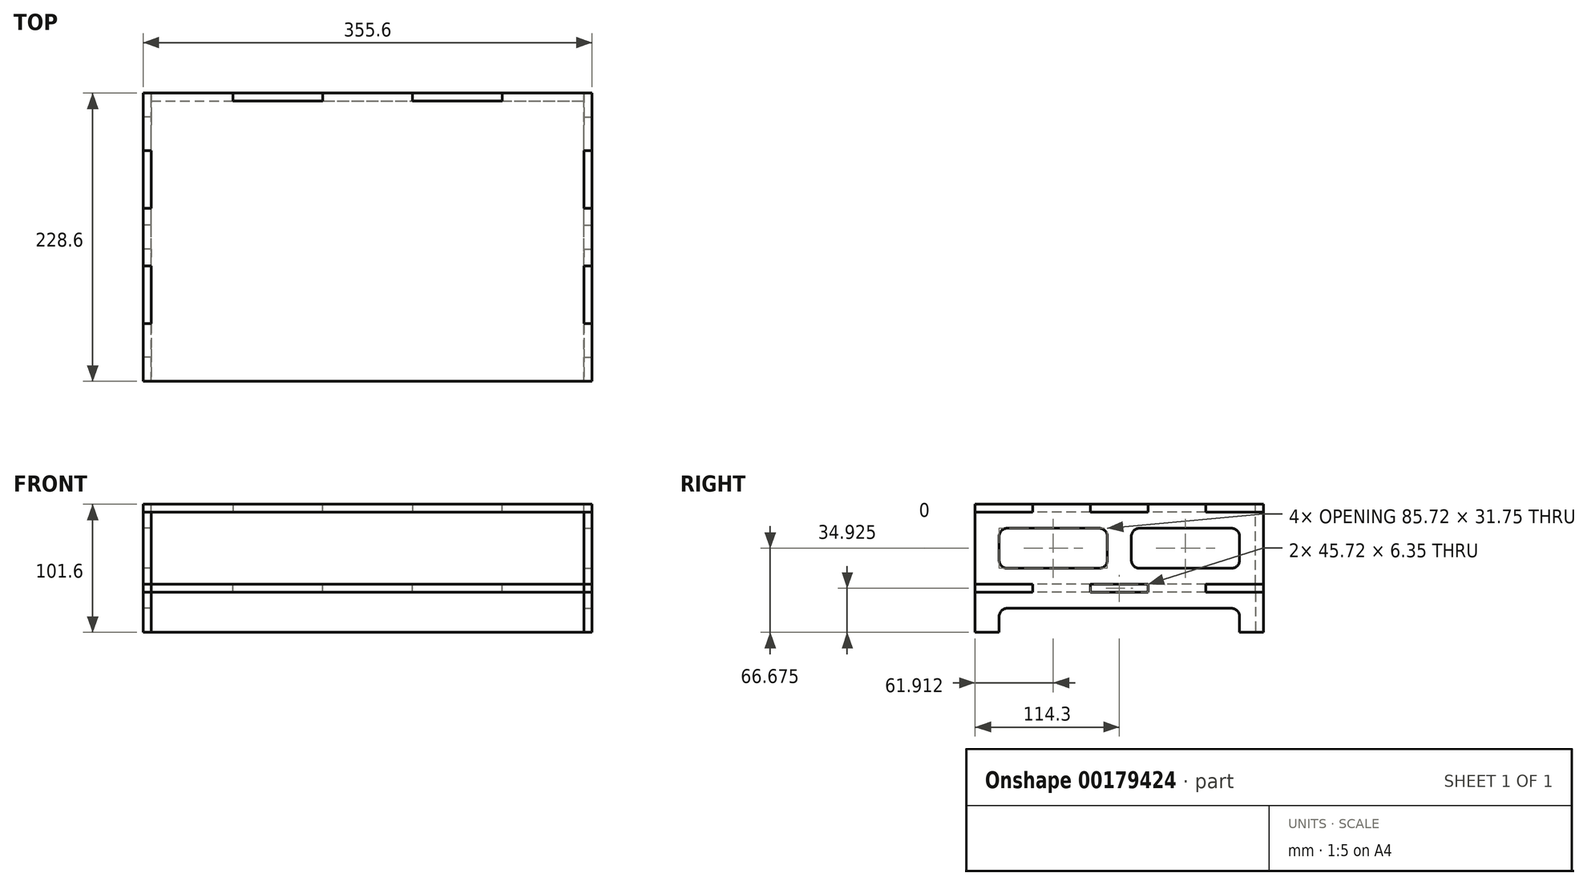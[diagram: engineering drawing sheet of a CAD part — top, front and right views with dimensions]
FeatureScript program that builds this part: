
annotation { "Feature Type Name" : "Feature", "Feature Type Description" : "" }
export const myFeature = defineFeature(function(context is Context, id is Id, definition is map)
    precondition{}
    {
        {
            var Q0;
            Q0=qCreatedBy(makeId("Top.planeOp"),FACE);
            var sketch = newSketch(context, id + "F0", { "sketchPlane" : qUnion([Q0])});
            skLineSegment(sketch, "E0.rect.bottom", {"start": v(177.8, -114.3) * mm, "end": v(-177.8, -114.3) * mm});
            skLineSegment(sketch, "E0.rect.top", {"start": v(177.8, 114.3) * mm, "end": v(-177.8, 114.3) * mm});
            skLineSegment(sketch, "E0.rect.left", {"start": v(177.8, -114.3) * mm, "end": v(177.8, 114.3) * mm});
            skLineSegment(sketch, "E0.rect.right", {"start": v(-177.8, -114.3) * mm, "end": v(-177.8, 114.3) * mm});
            skPoint(sketch, "E0.rect.middle", {"position": v(0, 0) * mm});
            skSolve(sketch);
        }
        {
            var Q0;
            Q0=qCreatedBy(makeId("Right.planeOp"),FACE);
            var sketch = newSketch(context, id + "F1", { "sketchPlane" : qUnion([Q0])});
            skLineSegment(sketch, "E1.0", {"start": v(-114.3, 0) * mm, "end": v(114.3, 0) * mm});
            skLineSegment(sketch, "E2", {"start": v(114.3, 0) * mm, "end": v(114.3, -101.6) * mm});
            skLineSegment(sketch, "E3", {"start": v(114.3, -101.6) * mm, "end": v(-114.3, -101.6) * mm});
            skLineSegment(sketch, "E4", {"start": v(-114.3, -101.6) * mm, "end": v(-114.3, 0) * mm});
            skLineSegment(sketch, "E5", {"start": v(-114.3, -63.5) * mm, "end": v(114.3, -63.5) * mm});
            skSolve(sketch);
        }
        {
            var Q0;
            Q0=sQuery(id+"F0.wireOp",EDGE,"E0.rect.top");
            cPlane(context, id + "F2", {"entities" : qUnion([Q0]), "cplaneType" : CPlaneType.LINE_ANGLE, "offset" : 152.4 * mm, "angle" : 0 * degree, "width" : 152.4 * mm, "height" : 152.4 * mm});
        }
        {
            var Q0;
            Q0=qCreatedBy(makeId("Top.planeOp"),FACE);
            var sketch = newSketch(context, id + "F3", { "sketchPlane" : qUnion([Q0])});
            skLineSegment(sketch, "E6.0", {"start": v(177.8, -114.3) * mm, "end": v(-177.8, -114.3) * mm});
            skLineSegment(sketch, "E7.0", {"start": v(-177.8, -114.3) * mm, "end": v(-177.8, -68.58) * mm});
            skLineSegment(sketch, "E8.0", {"start": v(177.8, -114.3) * mm, "end": v(177.8, -68.58) * mm});
            skLineSegment(sketch, "E9", {"start": v(-177.8, 114.3) * mm, "end": v(-177.8, 68.58) * mm});
            skLineSegment(sketch, "E10", {"start": v(-177.8, 68.58) * mm, "end": v(-171.45, 68.58) * mm});
            skLineSegment(sketch, "E11", {"start": v(-171.45, 68.58) * mm, "end": v(-171.45, 22.86) * mm});
            skLineSegment(sketch, "E12", {"start": v(-171.45, 22.86) * mm, "end": v(-177.8, 22.86) * mm});
            skLineSegment(sketch, "E13", {"start": v(-177.8, 22.86) * mm, "end": v(-177.8, -22.86) * mm});
            skLineSegment(sketch, "E14", {"start": v(-177.8, -22.86) * mm, "end": v(-171.45, -22.86) * mm});
            skLineSegment(sketch, "E15", {"start": v(-171.45, -22.86) * mm, "end": v(-171.45, -68.58) * mm});
            skLineSegment(sketch, "E16", {"start": v(-171.45, -68.58) * mm, "end": v(-177.8, -68.58) * mm});
            skLineSegment(sketch, "E17", {"start": v(-177.8, -68.58) * mm, "end": v(-177.8, -114.3) * mm});
            skLineSegment(sketch, "E18.trimOffspring", {"start": v(-177.8, 68.58) * mm, "end": v(-177.8, 114.3) * mm});
            skLineSegment(sketch, "E19.trimOffspring", {"start": v(-177.8, -22.86) * mm, "end": v(-177.8, 22.86) * mm});
            skLineSegment(sketch, "E20", {"start": v(-177.8, 114.3) * mm, "end": v(177.8, 114.3) * mm, "construction": true});
            skLineSegment(sketch, "E21", {"start": v(177.8, 114.3) * mm, "end": v(177.8, 68.58) * mm});
            skLineSegment(sketch, "E22", {"start": v(177.8, 68.58) * mm, "end": v(171.45, 68.58) * mm});
            skLineSegment(sketch, "E23", {"start": v(171.45, 68.58) * mm, "end": v(171.45, 22.86) * mm});
            skLineSegment(sketch, "E24", {"start": v(171.45, 22.86) * mm, "end": v(177.8, 22.86) * mm});
            skLineSegment(sketch, "E25", {"start": v(177.8, 22.86) * mm, "end": v(177.8, -22.86) * mm});
            skLineSegment(sketch, "E26", {"start": v(177.8, -22.86) * mm, "end": v(171.45, -22.86) * mm});
            skLineSegment(sketch, "E27", {"start": v(171.45, -22.86) * mm, "end": v(171.45, -68.58) * mm});
            skLineSegment(sketch, "E28", {"start": v(171.45, -68.58) * mm, "end": v(177.8, -68.58) * mm});
            skLineSegment(sketch, "E29", {"start": v(177.8, -68.58) * mm, "end": v(177.8, -114.3) * mm});
            skLineSegment(sketch, "E30.trimOffspring", {"start": v(177.8, 68.58) * mm, "end": v(177.8, 114.3) * mm});
            skLineSegment(sketch, "E31.trimOffspring", {"start": v(177.8, -22.86) * mm, "end": v(177.8, 22.86) * mm});
            skLineSegment(sketch, "E32", {"start": v(-106.68, 114.3) * mm, "end": v(-106.68, 107.95) * mm});
            skLineSegment(sketch, "E33", {"start": v(-106.68, 107.95) * mm, "end": v(-35.56, 107.95) * mm});
            skLineSegment(sketch, "E34", {"start": v(-35.56, 107.95) * mm, "end": v(-35.56, 114.3) * mm});
            skLineSegment(sketch, "E35", {"start": v(-35.56, 114.3) * mm, "end": v(35.56, 114.3) * mm});
            skLineSegment(sketch, "E36", {"start": v(35.56, 114.3) * mm, "end": v(35.56, 107.95) * mm});
            skLineSegment(sketch, "E37", {"start": v(35.56, 107.95) * mm, "end": v(106.68, 107.95) * mm});
            skLineSegment(sketch, "E38", {"start": v(106.68, 107.95) * mm, "end": v(106.68, 114.3) * mm});
            skLineSegment(sketch, "E39", {"start": v(-177.8, 114.3) * mm, "end": v(-106.68, 114.3) * mm});
            skLineSegment(sketch, "E40", {"start": v(106.68, 114.3) * mm, "end": v(177.8, 114.3) * mm});
            skSolve(sketch);
        }
        {
            var Q0;
            Q0=sQuery(id+"F0.wireOp",EDGE,"E0.rect.left");
            cPlane(context, id + "F4", {"entities" : qUnion([Q0]), "cplaneType" : CPlaneType.LINE_ANGLE, "offset" : 152.4 * mm, "angle" : 90 * degree, "width" : 152.4 * mm, "height" : 152.4 * mm});
        }
        {
            var Q0;
            Q0=sQuery(id+"F0.wireOp",EDGE,"E0.rect.right");
            cPlane(context, id + "F5", {"entities" : qUnion([Q0]), "cplaneType" : CPlaneType.LINE_ANGLE, "offset" : 152.4 * mm, "angle" : 90 * degree, "width" : 152.4 * mm, "height" : 152.4 * mm});
        }
        {
            var Q0;
            Q0=sQuery(id+"F1.wireOp",EDGE,"E5");
            cPlane(context, id + "F6", {"entities" : qUnion([Q0]), "cplaneType" : CPlaneType.LINE_ANGLE, "offset" : 152.4 * mm, "angle" : 0 * degree, "width" : 152.4 * mm, "height" : 152.4 * mm});
        }
        {
            var Q0;
            Q0=makeQuery(id+"F3.imprint","IMPRINT",FACE,{"disambiguationData":[TD([[makeQuery(id+"F3.imprint","IMPRINT",EDGE,{"derivedFrom":sQuery(id+"F3.wireOp",EDGE,"E6.0")}),-1.0]])]});
            extrude(context, id + "F7", {"entities" : qUnion([Q0]), "oppositeDirection" : true, "depth" : 6.35 * mm});
        }
        {
            var Q0;
            Q0=qCreatedBy(id+"F6.planeOp",FACE);
            var sketch = newSketch(context, id + "F8", { "sketchPlane" : qUnion([Q0])});
            skLineSegment(sketch, "E41.0", {"start": v(177.8, -114.3) * mm, "end": v(-177.8, -114.3) * mm});
            skLineSegment(sketch, "E41.1", {"start": v(-177.8, -114.3) * mm, "end": v(-177.8, -68.58) * mm});
            skLineSegment(sketch, "E41.2", {"start": v(177.8, -114.3) * mm, "end": v(177.8, -68.58) * mm});
            skLineSegment(sketch, "E41.3", {"start": v(-177.8, 114.3) * mm, "end": v(-177.8, 68.58) * mm});
            skLineSegment(sketch, "E41.4", {"start": v(-177.8, 68.58) * mm, "end": v(-171.45, 68.58) * mm});
            skLineSegment(sketch, "E41.5", {"start": v(-171.45, 68.58) * mm, "end": v(-171.45, 22.86) * mm});
            skLineSegment(sketch, "E41.6", {"start": v(-171.45, 22.86) * mm, "end": v(-177.8, 22.86) * mm});
            skLineSegment(sketch, "E41.7", {"start": v(-177.8, 22.86) * mm, "end": v(-177.8, -22.86) * mm});
            skLineSegment(sketch, "E41.8", {"start": v(-177.8, -22.86) * mm, "end": v(-171.45, -22.86) * mm});
            skLineSegment(sketch, "E41.9", {"start": v(-171.45, -22.86) * mm, "end": v(-171.45, -68.58) * mm});
            skLineSegment(sketch, "E41.10", {"start": v(-171.45, -68.58) * mm, "end": v(-177.8, -68.58) * mm});
            skLineSegment(sketch, "E41.11", {"start": v(-177.8, -68.58) * mm, "end": v(-177.8, -114.3) * mm});
            skLineSegment(sketch, "E41.12", {"start": v(-177.8, 68.58) * mm, "end": v(-177.8, 114.3) * mm});
            skLineSegment(sketch, "E41.13", {"start": v(-177.8, -22.86) * mm, "end": v(-177.8, 22.86) * mm});
            skLineSegment(sketch, "E41.14", {"start": v(-177.8, 68.58) * mm, "end": v(-177.8, 114.3) * mm});
            skLineSegment(sketch, "E41.16", {"start": v(177.8, 114.3) * mm, "end": v(177.8, 68.58) * mm});
            skLineSegment(sketch, "E41.17", {"start": v(177.8, 68.58) * mm, "end": v(171.45, 68.58) * mm});
            skLineSegment(sketch, "E41.18", {"start": v(171.45, 68.58) * mm, "end": v(171.45, 22.86) * mm});
            skLineSegment(sketch, "E41.19", {"start": v(171.45, 22.86) * mm, "end": v(177.8, 22.86) * mm});
            skLineSegment(sketch, "E41.20", {"start": v(177.8, 22.86) * mm, "end": v(177.8, -22.86) * mm});
            skLineSegment(sketch, "E41.21", {"start": v(177.8, -22.86) * mm, "end": v(171.45, -22.86) * mm});
            skLineSegment(sketch, "E41.22", {"start": v(171.45, -22.86) * mm, "end": v(171.45, -68.58) * mm});
            skLineSegment(sketch, "E41.23", {"start": v(171.45, -68.58) * mm, "end": v(177.8, -68.58) * mm});
            skLineSegment(sketch, "E41.24", {"start": v(177.8, -68.58) * mm, "end": v(177.8, -114.3) * mm});
            skLineSegment(sketch, "E41.25", {"start": v(177.8, 68.58) * mm, "end": v(177.8, 114.3) * mm});
            skLineSegment(sketch, "E41.26", {"start": v(177.8, -22.86) * mm, "end": v(177.8, 22.86) * mm});
            skLineSegment(sketch, "E41.27", {"start": v(-106.68, 114.3) * mm, "end": v(-106.68, 107.95) * mm});
            skLineSegment(sketch, "E41.28", {"start": v(-106.68, 107.95) * mm, "end": v(-35.56, 107.95) * mm});
            skLineSegment(sketch, "E41.29", {"start": v(-35.56, 107.95) * mm, "end": v(-35.56, 114.3) * mm});
            skLineSegment(sketch, "E41.30", {"start": v(-35.56, 114.3) * mm, "end": v(35.56, 114.3) * mm});
            skLineSegment(sketch, "E41.31", {"start": v(35.56, 114.3) * mm, "end": v(35.56, 107.95) * mm});
            skLineSegment(sketch, "E41.32", {"start": v(35.56, 107.95) * mm, "end": v(106.68, 107.95) * mm});
            skLineSegment(sketch, "E41.33", {"start": v(106.68, 107.95) * mm, "end": v(106.68, 114.3) * mm});
            skLineSegment(sketch, "E41.34", {"start": v(-177.8, 114.3) * mm, "end": v(-106.68, 114.3) * mm});
            skLineSegment(sketch, "E41.35", {"start": v(-35.56, 114.3) * mm, "end": v(35.56, 114.3) * mm});
            skLineSegment(sketch, "E41.36", {"start": v(106.68, 114.3) * mm, "end": v(177.8, 114.3) * mm});
            skSolve(sketch);
        }
        {
            var Q0;
            Q0=qSketchRegion(id+"F8",true);
            extrude(context, id + "F9", {"entities" : qUnion([Q0]), "oppositeDirection" : true, "depth" : 6.35 * mm});
        }
        {
            var Q0;
            Q0=qCreatedBy(id+"F4.planeOp",FACE);
            var sketch = newSketch(context, id + "F10", { "sketchPlane" : qUnion([Q0])});
            skLineSegment(sketch, "E42.0", {"start": v(-68.58, 0) * mm, "end": v(-22.86, 0) * mm});
            skLineSegment(sketch, "E42.1", {"start": v(22.86, 0) * mm, "end": v(68.58, 0) * mm});
            skLineSegment(sketch, "E42.2", {"start": v(114.3, -6.35) * mm, "end": v(114.3, -63.5) * mm});
            skLineSegment(sketch, "E42.3", {"start": v(114.3, -101.6) * mm, "end": v(95.25, -101.6) * mm});
            skLineSegment(sketch, "E42.4", {"start": v(-114.3, -101.6) * mm, "end": v(-114.3, -69.85) * mm});
            skLineSegment(sketch, "E42.5", {"start": v(-114.3, -63.5) * mm, "end": v(-68.58, -63.5) * mm});
            skLineSegment(sketch, "E43.0", {"start": v(-68.58, -6.35) * mm, "end": v(-68.58, 0) * mm});
            skLineSegment(sketch, "E43.1", {"start": v(-68.58, -6.35) * mm, "end": v(-114.3, -6.35) * mm});
            skLineSegment(sketch, "E43.2", {"start": v(-22.86, -6.35) * mm, "end": v(-22.86, 0) * mm});
            skLineSegment(sketch, "E43.3", {"start": v(-22.86, -6.35) * mm, "end": v(22.86, -6.35) * mm});
            skLineSegment(sketch, "E43.4", {"start": v(22.86, -6.35) * mm, "end": v(22.86, 0) * mm});
            skLineSegment(sketch, "E43.5", {"start": v(68.58, -6.35) * mm, "end": v(68.58, 0) * mm});
            skLineSegment(sketch, "E43.6", {"start": v(68.58, -6.35) * mm, "end": v(68.58, -6.35) * mm});
            skLineSegment(sketch, "E44.trimOffspring", {"start": v(-114.3, -63.5) * mm, "end": v(-114.3, -6.35) * mm});
            skLineSegment(sketch, "E45.trimOffspring", {"start": v(114.3, -69.85) * mm, "end": v(114.3, -101.6) * mm});
            skLineSegment(sketch, "E46.trimOffspring", {"start": v(68.58, -63.5) * mm, "end": v(114.3, -63.5) * mm});
            skLineSegment(sketch, "E47.trimOffspring", {"start": v(-22.86, -63.5) * mm, "end": v(22.86, -63.5) * mm});
            skLineSegment(sketch, "E48", {"start": v(-114.3, -101.6) * mm, "end": v(-95.25, -101.6) * mm});
            skLineSegment(sketch, "E49", {"start": v(-95.25, -101.6) * mm, "end": v(-95.25, -88.9) * mm});
            skLineSegment(sketch, "E50", {"start": v(-88.9, -82.55) * mm, "end": v(88.9, -82.55) * mm});
            skLineSegment(sketch, "E51", {"start": v(95.25, -88.9) * mm, "end": v(95.25, -101.6) * mm});
            skLineSegment(sketch, "E52", {"start": v(95.25, -101.6) * mm, "end": v(114.3, -101.6) * mm});
            skLineSegment(sketch, "E53.trimOffspring", {"start": v(-95.25, -101.6) * mm, "end": v(-114.3, -101.6) * mm});
            skPoint(sketch, "E54.visualSharp", {"position": v(-95.25, -82.55) * mm});
            skArc(sketch, "E54.filletArc", {"start": v(-88.9, -82.55) * mm, "mid": v(-93.4, -84.4) * mm, "end": v(-95.25, -88.9) * mm});
            skPoint(sketch, "E55.visualSharp", {"position": v(95.25, -82.55) * mm});
            skArc(sketch, "E55.filletArc", {"start": v(95.25, -88.9) * mm, "mid": v(93.4, -84.4) * mm, "end": v(88.9, -82.55) * mm});
            skLineSegment(sketch, "E56.bottom", {"start": v(-88.9, -19.05) * mm, "end": v(-15.87, -19.05) * mm});
            skLineSegment(sketch, "E56.top", {"start": v(-88.9, -50.8) * mm, "end": v(-15.87, -50.8) * mm});
            skLineSegment(sketch, "E56.left", {"start": v(-95.25, -25.4) * mm, "end": v(-95.25, -44.45) * mm});
            skLineSegment(sketch, "E56.right", {"start": v(95.25, -25.4) * mm, "end": v(95.25, -44.45) * mm});
            skPoint(sketch, "E57.visualSharp", {"position": v(-95.25, -19.05) * mm});
            skArc(sketch, "E57.filletArc", {"start": v(-88.9, -19.05) * mm, "mid": v(-93.4, -20.9) * mm, "end": v(-95.25, -25.4) * mm});
            skPoint(sketch, "E58.visualSharp", {"position": v(95.25, -19.05) * mm});
            skArc(sketch, "E58.filletArc", {"start": v(95.25, -25.4) * mm, "mid": v(93.4, -20.9) * mm, "end": v(88.9, -19.05) * mm});
            skPoint(sketch, "E59.visualSharp", {"position": v(95.25, -50.8) * mm});
            skArc(sketch, "E59.filletArc", {"start": v(88.9, -50.8) * mm, "mid": v(93.4, -48.94) * mm, "end": v(95.25, -44.45) * mm});
            skPoint(sketch, "E60.visualSharp", {"position": v(-95.25, -50.8) * mm});
            skArc(sketch, "E60.filletArc", {"start": v(-95.25, -44.45) * mm, "mid": v(-93.4, -48.94) * mm, "end": v(-88.9, -50.8) * mm});
            skLineSegment(sketch, "E61", {"start": v(9.53, -25.4) * mm, "end": v(9.53, -44.45) * mm});
            skLineSegment(sketch, "E62", {"start": v(-9.52, -44.45) * mm, "end": v(-9.52, -25.4) * mm});
            skLineSegment(sketch, "E63.trimOffspring", {"start": v(15.88, -19.05) * mm, "end": v(88.9, -19.05) * mm});
            skLineSegment(sketch, "E64.trimOffspring", {"start": v(15.88, -50.8) * mm, "end": v(88.9, -50.8) * mm});
            skPoint(sketch, "E65.visualSharp", {"position": v(-9.52, -19.05) * mm});
            skArc(sketch, "E65.filletArc", {"start": v(-9.52, -25.4) * mm, "mid": v(-11.38, -20.9) * mm, "end": v(-15.87, -19.05) * mm});
            skPoint(sketch, "E66.visualSharp", {"position": v(-9.52, -50.8) * mm});
            skArc(sketch, "E66.filletArc", {"start": v(-15.87, -50.8) * mm, "mid": v(-11.38, -48.94) * mm, "end": v(-9.52, -44.45) * mm});
            skPoint(sketch, "E67.visualSharp", {"position": v(9.53, -19.05) * mm});
            skArc(sketch, "E67.filletArc", {"start": v(15.88, -19.05) * mm, "mid": v(11.38, -20.9) * mm, "end": v(9.53, -25.4) * mm});
            skPoint(sketch, "E68.visualSharp", {"position": v(9.53, -50.8) * mm});
            skArc(sketch, "E68.filletArc", {"start": v(9.53, -44.45) * mm, "mid": v(11.38, -48.94) * mm, "end": v(15.88, -50.8) * mm});
            skLineSegment(sketch, "E69.0", {"start": v(68.58, -6.35) * mm, "end": v(114.3, -6.35) * mm});
            skLineSegment(sketch, "E70.0", {"start": v(-68.58, -69.85) * mm, "end": v(-68.58, -63.5) * mm});
            skLineSegment(sketch, "E70.1", {"start": v(-68.58, -69.85) * mm, "end": v(-114.3, -69.85) * mm});
            skLineSegment(sketch, "E70.2", {"start": v(-114.3, -69.85) * mm, "end": v(-114.3, -63.5) * mm});
            skLineSegment(sketch, "E70.3", {"start": v(-22.86, -69.85) * mm, "end": v(-22.86, -63.5) * mm});
            skLineSegment(sketch, "E70.4", {"start": v(-22.86, -69.85) * mm, "end": v(22.86, -69.85) * mm});
            skLineSegment(sketch, "E70.5", {"start": v(22.86, -69.85) * mm, "end": v(22.86, -63.5) * mm});
            skLineSegment(sketch, "E70.6", {"start": v(68.58, -69.85) * mm, "end": v(114.3, -69.85) * mm});
            skLineSegment(sketch, "E70.7", {"start": v(68.58, -69.85) * mm, "end": v(68.58, -63.5) * mm});
            skSolve(sketch);
        }
        {
            var Q0;
            Q0=qSketchRegion(id+"F10",true);
            extrude(context, id + "F11", {"entities" : qUnion([Q0]), "oppositeDirection" : true, "depth" : 6.35 * mm});
        }
        {
            var Q0;
            Q0=qCreatedBy(id+"F5.planeOp",FACE);
            var sketch = newSketch(context, id + "F12", { "sketchPlane" : qUnion([Q0])});
            skLineSegment(sketch, "E71.0", {"start": v(-68.58, 0) * mm, "end": v(-22.86, 0) * mm});
            skLineSegment(sketch, "E71.1", {"start": v(22.86, 0) * mm, "end": v(68.58, 0) * mm});
            skLineSegment(sketch, "E71.2", {"start": v(114.3, -6.35) * mm, "end": v(114.3, -63.5) * mm});
            skLineSegment(sketch, "E71.3", {"start": v(114.3, -101.6) * mm, "end": v(95.25, -101.6) * mm});
            skLineSegment(sketch, "E71.4", {"start": v(-114.3, -101.6) * mm, "end": v(-114.3, -69.85) * mm});
            skLineSegment(sketch, "E71.5", {"start": v(-114.3, -63.5) * mm, "end": v(-68.58, -63.5) * mm});
            skLineSegment(sketch, "E71.6", {"start": v(-68.58, -6.35) * mm, "end": v(-68.58, 0) * mm});
            skLineSegment(sketch, "E71.7", {"start": v(-68.58, -6.35) * mm, "end": v(-114.3, -6.35) * mm});
            skLineSegment(sketch, "E71.8", {"start": v(-22.86, -6.35) * mm, "end": v(-22.86, 0) * mm});
            skLineSegment(sketch, "E71.9", {"start": v(-22.86, -6.35) * mm, "end": v(22.86, -6.35) * mm});
            skLineSegment(sketch, "E71.10", {"start": v(22.86, -6.35) * mm, "end": v(22.86, 0) * mm});
            skLineSegment(sketch, "E71.11", {"start": v(68.58, -6.35) * mm, "end": v(68.58, 0) * mm});
            skPoint(sketch, "E71.12", {"position": v(68.58, -6.35) * mm});
            skLineSegment(sketch, "E71.13", {"start": v(-114.3, -63.5) * mm, "end": v(-114.3, -6.35) * mm});
            skLineSegment(sketch, "E71.14", {"start": v(114.3, -69.85) * mm, "end": v(114.3, -101.6) * mm});
            skLineSegment(sketch, "E71.15", {"start": v(22.86, 0) * mm, "end": v(68.58, 0) * mm});
            skLineSegment(sketch, "E71.16", {"start": v(68.58, -63.5) * mm, "end": v(114.3, -63.5) * mm});
            skLineSegment(sketch, "E71.17", {"start": v(-22.86, -63.5) * mm, "end": v(22.86, -63.5) * mm});
            skLineSegment(sketch, "E71.18", {"start": v(-114.3, -101.6) * mm, "end": v(-95.25, -101.6) * mm});
            skLineSegment(sketch, "E71.19", {"start": v(-95.25, -101.6) * mm, "end": v(-95.25, -88.9) * mm});
            skLineSegment(sketch, "E71.20", {"start": v(-88.9, -82.55) * mm, "end": v(88.9, -82.55) * mm});
            skLineSegment(sketch, "E71.21", {"start": v(95.25, -88.9) * mm, "end": v(95.25, -101.6) * mm});
            skLineSegment(sketch, "E71.22", {"start": v(95.25, -101.6) * mm, "end": v(114.3, -101.6) * mm});
            skLineSegment(sketch, "E71.23", {"start": v(-95.25, -101.6) * mm, "end": v(-114.3, -101.6) * mm});
            skPoint(sketch, "E71.24", {"position": v(-95.25, -82.55) * mm});
            skArc(sketch, "E71.25", {"start": v(-88.9, -82.55) * mm, "mid": v(-93.4, -84.4) * mm, "end": v(-95.25, -88.9) * mm});
            skPoint(sketch, "E71.26", {"position": v(95.25, -82.55) * mm});
            skArc(sketch, "E71.27", {"start": v(95.25, -88.9) * mm, "mid": v(93.4, -84.4) * mm, "end": v(88.9, -82.55) * mm});
            skLineSegment(sketch, "E71.28", {"start": v(-88.9, -19.05) * mm, "end": v(-15.87, -19.05) * mm});
            skLineSegment(sketch, "E71.29", {"start": v(-88.9, -50.8) * mm, "end": v(-15.87, -50.8) * mm});
            skLineSegment(sketch, "E71.30", {"start": v(-95.25, -25.4) * mm, "end": v(-95.25, -44.45) * mm});
            skLineSegment(sketch, "E71.31", {"start": v(95.25, -25.4) * mm, "end": v(95.25, -44.45) * mm});
            skPoint(sketch, "E71.32", {"position": v(-95.25, -19.05) * mm});
            skArc(sketch, "E71.33", {"start": v(-88.9, -19.05) * mm, "mid": v(-93.4, -20.9) * mm, "end": v(-95.25, -25.4) * mm});
            skPoint(sketch, "E71.34", {"position": v(95.25, -19.05) * mm});
            skArc(sketch, "E71.35", {"start": v(95.25, -25.4) * mm, "mid": v(93.4, -20.9) * mm, "end": v(88.9, -19.05) * mm});
            skPoint(sketch, "E71.36", {"position": v(95.25, -50.8) * mm});
            skArc(sketch, "E71.37", {"start": v(88.9, -50.8) * mm, "mid": v(93.4, -48.94) * mm, "end": v(95.25, -44.45) * mm});
            skPoint(sketch, "E71.38", {"position": v(-95.25, -50.8) * mm});
            skArc(sketch, "E71.39", {"start": v(-95.25, -44.45) * mm, "mid": v(-93.4, -48.94) * mm, "end": v(-88.9, -50.8) * mm});
            skLineSegment(sketch, "E71.40", {"start": v(9.53, -25.4) * mm, "end": v(9.53, -44.45) * mm});
            skLineSegment(sketch, "E71.41", {"start": v(-9.52, -44.45) * mm, "end": v(-9.52, -25.4) * mm});
            skLineSegment(sketch, "E71.42", {"start": v(15.88, -19.05) * mm, "end": v(88.9, -19.05) * mm});
            skLineSegment(sketch, "E71.43", {"start": v(15.88, -50.8) * mm, "end": v(88.9, -50.8) * mm});
            skPoint(sketch, "E71.44", {"position": v(-9.52, -19.05) * mm});
            skArc(sketch, "E71.45", {"start": v(-9.52, -25.4) * mm, "mid": v(-11.38, -20.9) * mm, "end": v(-15.87, -19.05) * mm});
            skPoint(sketch, "E71.46", {"position": v(-9.52, -50.8) * mm});
            skArc(sketch, "E71.47", {"start": v(-15.87, -50.8) * mm, "mid": v(-11.38, -48.94) * mm, "end": v(-9.52, -44.45) * mm});
            skPoint(sketch, "E71.48", {"position": v(9.53, -19.05) * mm});
            skArc(sketch, "E71.49", {"start": v(15.88, -19.05) * mm, "mid": v(11.38, -20.9) * mm, "end": v(9.53, -25.4) * mm});
            skPoint(sketch, "E71.50", {"position": v(9.53, -50.8) * mm});
            skArc(sketch, "E71.51", {"start": v(9.53, -44.45) * mm, "mid": v(11.38, -48.94) * mm, "end": v(15.88, -50.8) * mm});
            skLineSegment(sketch, "E71.52", {"start": v(68.58, -6.35) * mm, "end": v(114.3, -6.35) * mm});
            skLineSegment(sketch, "E71.53", {"start": v(-68.58, -69.85) * mm, "end": v(-68.58, -63.5) * mm});
            skLineSegment(sketch, "E71.54", {"start": v(-68.58, -69.85) * mm, "end": v(-114.3, -69.85) * mm});
            skLineSegment(sketch, "E71.55", {"start": v(-114.3, -69.85) * mm, "end": v(-114.3, -63.5) * mm});
            skLineSegment(sketch, "E71.56", {"start": v(-22.86, -69.85) * mm, "end": v(-22.86, -63.5) * mm});
            skLineSegment(sketch, "E71.57", {"start": v(-22.86, -69.85) * mm, "end": v(22.86, -69.85) * mm});
            skLineSegment(sketch, "E71.58", {"start": v(22.86, -69.85) * mm, "end": v(22.86, -63.5) * mm});
            skLineSegment(sketch, "E71.59", {"start": v(68.58, -69.85) * mm, "end": v(114.3, -69.85) * mm});
            skLineSegment(sketch, "E71.60", {"start": v(68.58, -69.85) * mm, "end": v(68.58, -63.5) * mm});
            skSolve(sketch);
        }
        {
            var Q0;
            Q0=qSketchRegion(id+"F12",true);
            extrude(context, id + "F13", {"entities" : qUnion([Q0]), "depth" : 6.35 * mm});
        }
        {
            var Q0;
            Q0=qCreatedBy(id+"F2.planeOp",FACE);
            var sketch = newSketch(context, id + "F14", { "sketchPlane" : qUnion([Q0])});
            skPoint(sketch, "E72.0", {"position": v(171.45, -6.35) * mm});
            skPoint(sketch, "E72.1", {"position": v(171.45, -63.5) * mm});
            skPoint(sketch, "E72.4", {"position": v(171.45, -69.85) * mm});
            skPoint(sketch, "E72.7", {"position": v(171.45, -101.6) * mm});
            skPoint(sketch, "E72.8", {"position": v(106.68, -6.35) * mm});
            skPoint(sketch, "E72.9", {"position": v(35.56, -6.35) * mm});
            skPoint(sketch, "E72.10", {"position": v(-35.56, -6.35) * mm});
            skPoint(sketch, "E72.11", {"position": v(-106.68, -6.35) * mm});
            skPoint(sketch, "E72.12", {"position": v(-106.68, -63.5) * mm});
            skPoint(sketch, "E72.13", {"position": v(-106.68, -69.85) * mm});
            skPoint(sketch, "E72.14", {"position": v(-35.56, -69.85) * mm});
            skPoint(sketch, "E72.15", {"position": v(-35.56, -63.5) * mm});
            skPoint(sketch, "E72.16", {"position": v(35.56, -63.5) * mm});
            skPoint(sketch, "E72.17", {"position": v(35.56, -69.85) * mm});
            skPoint(sketch, "E72.18", {"position": v(106.68, -69.85) * mm});
            skPoint(sketch, "E72.19", {"position": v(106.68, -63.5) * mm});
            skLineSegment(sketch, "E73", {"start": v(171.45, -101.6) * mm, "end": v(171.45, -69.85) * mm});
            skLineSegment(sketch, "E74", {"start": v(106.68, -69.85) * mm, "end": v(106.68, -63.5) * mm});
            skLineSegment(sketch, "E75", {"start": v(171.45, -63.5) * mm, "end": v(171.45, -6.35) * mm});
            skLineSegment(sketch, "E76", {"start": v(106.68, -6.35) * mm, "end": v(171.45, -6.35) * mm});
            skLineSegment(sketch, "E77", {"start": v(171.45, -69.85) * mm, "end": v(106.68, -69.85) * mm});
            skLineSegment(sketch, "E78", {"start": v(106.68, -63.5) * mm, "end": v(171.45, -63.5) * mm});
            skLineSegment(sketch, "E79", {"start": v(106.68, -6.35) * mm, "end": v(106.68, 0) * mm});
            skLineSegment(sketch, "E80", {"start": v(106.68, 0) * mm, "end": v(35.56, 0) * mm});
            skLineSegment(sketch, "E81", {"start": v(35.56, 0) * mm, "end": v(35.56, -6.35) * mm});
            skLineSegment(sketch, "E82", {"start": v(35.56, -6.35) * mm, "end": v(-35.56, -6.35) * mm});
            skLineSegment(sketch, "E83", {"start": v(-35.56, -6.35) * mm, "end": v(-35.56, 0) * mm});
            skLineSegment(sketch, "E84", {"start": v(-35.56, 0) * mm, "end": v(-106.68, 0) * mm});
            skLineSegment(sketch, "E85", {"start": v(-106.68, 0) * mm, "end": v(-106.68, -6.35) * mm});
            skLineSegment(sketch, "E86", {"start": v(-106.68, -63.5) * mm, "end": v(-106.68, -69.85) * mm});
            skLineSegment(sketch, "E87", {"start": v(35.56, -63.5) * mm, "end": v(35.56, -69.85) * mm});
            skLineSegment(sketch, "E88", {"start": v(35.56, -69.85) * mm, "end": v(-35.56, -69.85) * mm});
            skLineSegment(sketch, "E89", {"start": v(-35.56, -63.5) * mm, "end": v(-35.56, -69.85) * mm});
            skLineSegment(sketch, "E90", {"start": v(-35.56, -63.5) * mm, "end": v(35.56, -63.5) * mm});
            skPoint(sketch, "E91.orphan", {"position": v(177.8, 0) * mm});
            skPoint(sketch, "E92.orphan", {"position": v(-177.8, 0) * mm});
            skLineSegment(sketch, "E93.0", {"start": v(-171.45, -6.35) * mm, "end": v(-106.68, -6.35) * mm});
            skLineSegment(sketch, "E93.1", {"start": v(-171.45, -6.35) * mm, "end": v(-171.45, -63.5) * mm});
            skLineSegment(sketch, "E93.2", {"start": v(-171.45, -63.5) * mm, "end": v(-106.68, -63.5) * mm});
            skLineSegment(sketch, "E93.3", {"start": v(-171.45, -69.85) * mm, "end": v(-106.68, -69.85) * mm});
            skLineSegment(sketch, "E93.4", {"start": v(-171.45, -69.85) * mm, "end": v(-171.45, -101.6) * mm});
            skPoint(sketch, "E94.orphan", {"position": v(-177.8, -6.35) * mm});
            skPoint(sketch, "E95.orphan", {"position": v(-177.8, -63.5) * mm});
            skPoint(sketch, "E96.orphan", {"position": v(-177.8, -69.85) * mm});
            skLineSegment(sketch, "E97", {"start": v(-171.45, -101.6) * mm, "end": v(171.45, -101.6) * mm});
            skSolve(sketch);
        }
        {
            var Q0;
            Q0=qSketchRegion(id+"F14",true);
            extrude(context, id + "F15", {"entities" : qUnion([Q0]), "depth" : 6.35 * mm});
        }
    });
